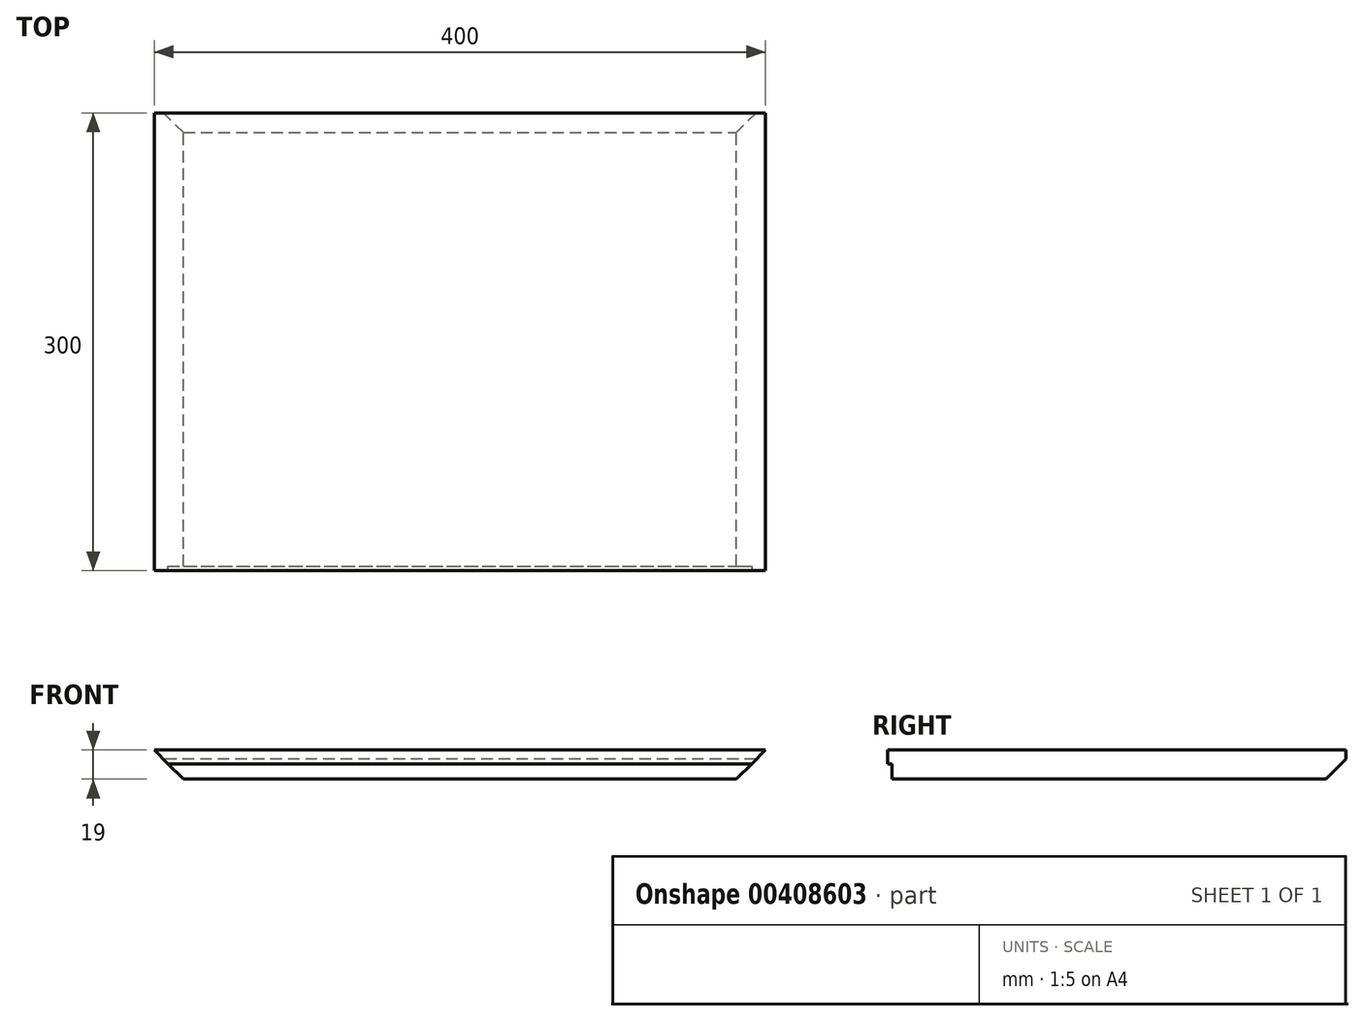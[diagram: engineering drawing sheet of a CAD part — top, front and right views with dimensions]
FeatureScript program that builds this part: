
annotation { "Feature Type Name" : "Feature", "Feature Type Description" : "" }
export const myFeature = defineFeature(function(context is Context, id is Id, definition is map)
    precondition{}
    {
        {
            var Q0;
            Q0=qCreatedBy(makeId("Front.planeOp"),FACE);
            var sketch = newSketch(context, id + "F0", { "sketchPlane" : qUnion([Q0])});
            skLineSegment(sketch, "E0", {"start": v(0, 0) * mm, "end": v(362, 0) * mm});
            skLineSegment(sketch, "E1", {"start": v(362, 0) * mm, "end": v(381, 19) * mm});
            skLineSegment(sketch, "E2", {"start": v(381, 19) * mm, "end": v(-19, 19) * mm});
            skLineSegment(sketch, "E3", {"start": v(-19, 19) * mm, "end": v(0, 0) * mm});
            skSolve(sketch);
        }
        {
            var Q0;
            Q0=makeQuery(id+"F0.imprint","IMPRINT",FACE,{"disambiguationData":[TD([[makeQuery(id+"F0.imprint","IMPRINT",EDGE,{"derivedFrom":sQuery(id+"F0.wireOp",EDGE,"E0")}),1.0]])]});
            extrude(context, id + "F1", {"entities" : qUnion([Q0]), "depth" : 300 * mm});
        }
        {
            var Q0;
            Q0=makeQuery(id+"F1.opExtrude","CAP_EDGE",EDGE,{"disambiguationData":[OSD([sQuery(id+"F0.wireOp",EDGE,"E0")])],"isStart":true});
            chamfer(context, id + "F2", {"entities" : qUnion([Q0]), "width" : 13 * mm, "tangentPropagation" : true});
        }
        {
            var Q0;
            Q0=makeQuery(id+"F1.opExtrude","CAP_FACE",FACE,{"disambiguationData":[OSD([sQuery(id+"F0.wireOp",EDGE,"E0"),sQuery(id+"F0.wireOp",EDGE,"E1"),sQuery(id+"F0.wireOp",EDGE,"E2"),sQuery(id+"F0.wireOp",EDGE,"E3")])],"isStart":false});
            var sketch = newSketch(context, id + "F3", { "sketchPlane" : qUnion([Q0])});
            skLineSegment(sketch, "E4.bottom", {"start": v(-20, 10) * mm, "end": v(380, 10) * mm});
            skLineSegment(sketch, "E4.top", {"start": v(-20, 0) * mm, "end": v(380, 0) * mm});
            skLineSegment(sketch, "E4.left", {"start": v(-20, 10) * mm, "end": v(-20, 0) * mm});
            skLineSegment(sketch, "E4.right", {"start": v(380, 10) * mm, "end": v(380, 0) * mm});
            skSolve(sketch);
        }
        {
            var Q0;
            Q0 = qSketchRegion(id + "F3", true);
            extrude(context, id + "F4", {"entities" : qUnion([Q0]), "operationType" : NewBodyOperationType.REMOVE, "oppositeDirection" : true, "depth" : 3 * mm});
        }
    });
